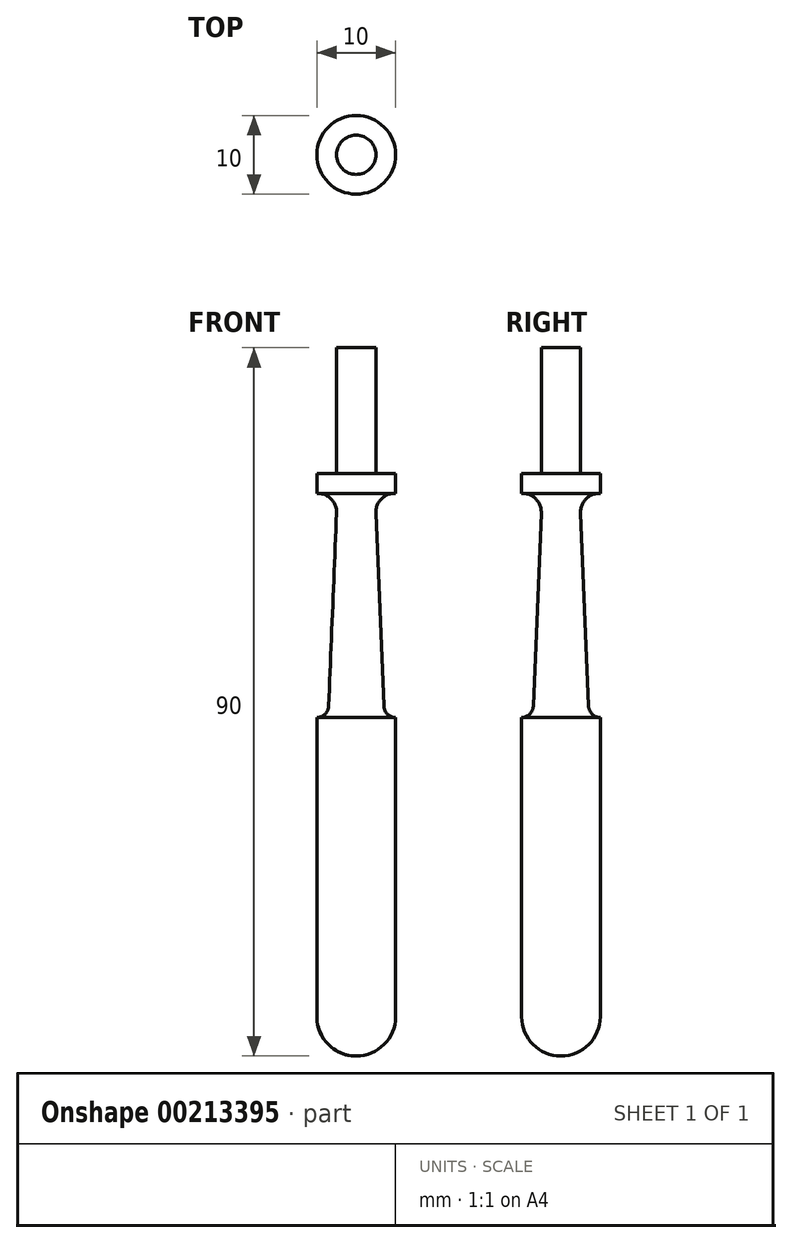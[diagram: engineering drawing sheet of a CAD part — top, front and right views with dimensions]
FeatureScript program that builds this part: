
annotation { "Feature Type Name" : "Feature", "Feature Type Description" : "" }
export const myFeature = defineFeature(function(context is Context, id is Id, definition is map)
    precondition{}
    {
        {
            var Q0;
            Q0=qCreatedBy(makeId("Front.planeOp"),FACE);
            var sketch = newSketch(context, id + "F0", { "sketchPlane" : qUnion([Q0])});
            skLineSegment(sketch, "E0", {"start": v(-48.43, -43.52) * mm, "end": v(-48.43, -5.52) * mm});
            skLineSegment(sketch, "E1", {"start": v(-43.43, -43.52) * mm, "end": v(-43.43, 22.98) * mm});
            skLineSegment(sketch, "E2", {"start": v(-45.93, 20.48) * mm, "end": v(-46.93, -4.02) * mm});
            skArc(sketch, "E3", {"start": v(-45.93, 20.48) * mm, "mid": v(-46.63, 22.28) * mm, "end": v(-48.43, 22.98) * mm});
            skArc(sketch, "E4", {"start": v(-46.93, -4.02) * mm, "mid": v(-47.39, -5.06) * mm, "end": v(-48.43, -5.52) * mm});
            skLineSegment(sketch, "E5", {"start": v(-43.43, -43.52) * mm, "end": v(-43.43, -48.52) * mm});
            skArc(sketch, "E6", {"start": v(-48.43, -43.52) * mm, "mid": v(-46.97, -47.06) * mm, "end": v(-43.43, -48.52) * mm});
            skLineSegment(sketch, "E7", {"start": v(-48.43, 22.98) * mm, "end": v(-48.43, 25.48) * mm});
            skLineSegment(sketch, "E8", {"start": v(-43.43, 25.48) * mm, "end": v(-43.43, 22.98) * mm});
            skLineSegment(sketch, "E9", {"start": v(-45.93, 25.48) * mm, "end": v(-45.93, 41.48) * mm});
            skLineSegment(sketch, "E10", {"start": v(-45.93, 41.48) * mm, "end": v(-43.43, 41.48) * mm});
            skLineSegment(sketch, "E11", {"start": v(-43.43, 41.48) * mm, "end": v(-43.43, 25.48) * mm});
            skLineSegment(sketch, "E12", {"start": v(-48.43, 25.48) * mm, "end": v(-45.93, 25.48) * mm});
            skSolve(sketch);
        }
        {
            var Q0;
            Q0 = qSketchRegion(id + "F0", true);
            var Q1;
            Q1=sQuery(id+"F0.wireOp",EDGE,"E1");
            revolve(context, id + "F1", {"entities" : qUnion([Q0]), "axis" : qUnion([Q1]), "revolveType" : RevolveType.FULL});
        }
    });
